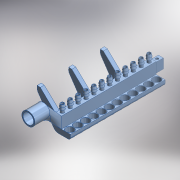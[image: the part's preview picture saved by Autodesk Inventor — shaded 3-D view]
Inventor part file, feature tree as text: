
AUTODESK INVENTOR PART (.ipt)
format: ipt  version: 2018 (Build 220112000, 112)  size: 669,184 bytes
history: native  units: in
note: dims shown in document units (in); Inventor stores cm internally (conversion verified against a paired STEP export)
features: other x13, extrude x7, pattern_linear x4, fillet x4, loft x2, projected_geometry x1, sketch x1
ambient origin geometry x8: Origin, YZ Plane, XZ Plane, XY Plane, X Axis, Y Axis, Z Axis, Center Point
bodies: Body1 (feature_tree)
feature tree (32):
  other  "CrossSection1"
  other  "Silicone Fitting Plane"
  other  "Cap Plane"
  other  "Base Sketch"
  extrude  "Base"  Depth=0.315in
  extrude  "Lip"  Depth=0.315in
  extrude  "Tube Socket"  Depth=0.315in
  pattern_linear  "Tube Socket Repetition"  Spacing1=0.0197in  [1 undecoded]
  other  "Silicone Fitting"
  pattern_linear  "Silicone Fitting Repetion"  Spacing1=0.5906in  [1 undecoded]
  extrude  "Coupling"  [1 undecoded]
  extrude  "Airflow Cut"  TaperAngle=0.0deg  [1 undecoded]
  pattern_linear  "Airflow Cut Repetition"  Spacing1=90.0deg  [1 undecoded]
  other  "Mouthpiece Adapter Plane"
  other  "Mouthpiece Adapter Loft To"
  loft  "Mouthpiece Adapter Outer"
  loft  "Moutpiece Adapter Inner"
  extrude  "Mouthpiece"  Depth=0.315in
  other  "Rule Fillet2"
  extrude  "Arm"  Depth=0.3214in
  fillet  "Fillet1"  [1 undecoded]
  fillet  "Fillet4"  Radius=0.7874in
  fillet  "Fillet6"  Radius=0.1607in
  pattern_linear  "Rectangular Pattern9"  Count1=3  [1 undecoded]
  fillet  "Fillet5"  [1 undecoded]
  other  "Silicone Fitting Sketch"
  other  "Airflow Cut Sketch"
  projected_geometry  "Projected Loop7"
  other  "Coupling Sketch"
  other  "Lip Sketch"
  sketch  "Sketch23"  dims[d87=0.0197in d88=0.0787in d89=-1.0625in d90=0.7874in d1=0.0591in d2=0.0591in d3=0.0591in d4=0.0197in d5=0.5906in d6=-0.2067in d8=0.0in d111=90.0deg d112=0.1181in d9=0.0in d12=-4.9606in d13=0.5906in d14=0.3214in d15=0.0in d122=0.7874in d124=0.1607in d125=1.1811in d128=0.0in d129=90.0deg d130=0.0in d131=90.0deg d132=0.0in d133=90.0deg d134=0.0in d135=90.0deg d136=0.7874in d137=0.0in d138=0.5512in d139=0.689in d140=0.7874in d141=0.0591in d142=0.0295in d143=0.0295in d144=0.0295in d145=0.0295in d146=0.0295in d147=0.0295in d148=0.0591in d155=5.1181in d157=0.4134in d158=4.7244in d160=0.4134in d161=4.9606in d163=0.3214in d164=0.0in d165=0.4724in d166=0.0in d167=0.3937in d168=0.2067in d169=0.2362in d170=0.3937in d171=0.0in d172=4.7244in d174=0.4134in d188=0.0157in d189=0.3214in d190=0.5906in d191=0.8661in d193=0.7874in d194=0.748in d197=0.1575in d200=0.2067in d201=0.0in d202=1.1811in d204=1.6535in d206=0.1181in d207=0.315in d209=0.315in d210=0.0481in]
  other  "Arm Sketch"
note: 8 required parameter values undecoded (feature->parameter linkage not recoverable at this tier; creation-order binding heuristic only, values carry confidence <= 0.55)
